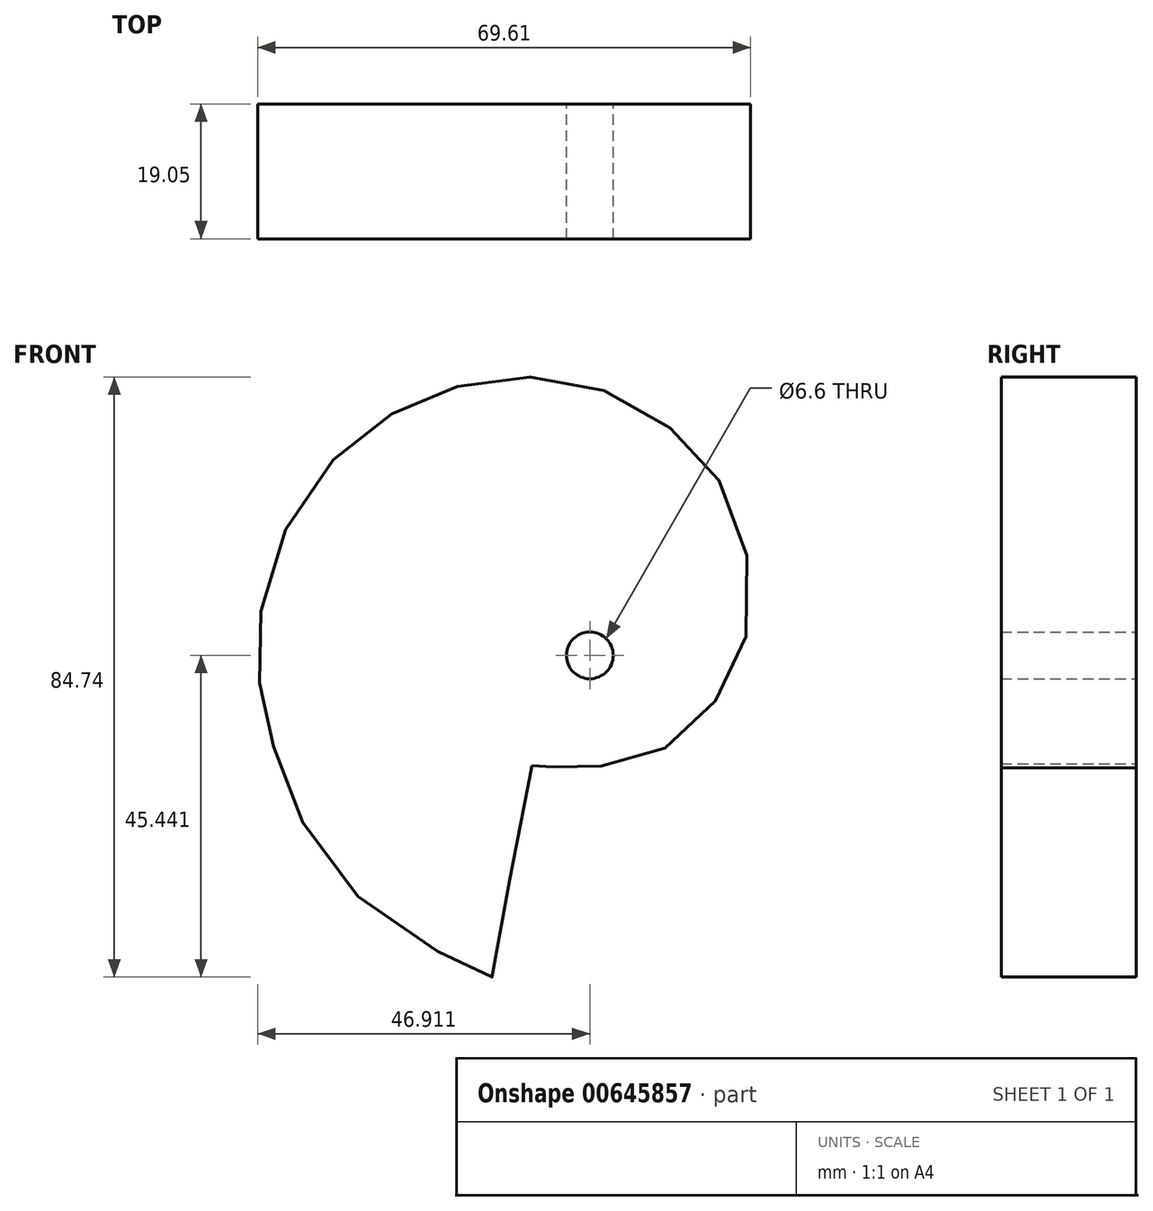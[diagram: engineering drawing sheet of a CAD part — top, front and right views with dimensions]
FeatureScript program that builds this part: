
annotation { "Feature Type Name" : "Feature", "Feature Type Description" : "" }
export const myFeature = defineFeature(function(context is Context, id is Id, definition is map)
    precondition{}
    {
        {
            var Q0;
            Q0=qCreatedBy(makeId("Front.planeOp"),FACE);
            var sketch = newSketch(context, id + "F0", { "sketchPlane" : qUnion([Q0])});
            skFitSpline(sketch, "E0", {"points": [v(-20.31, -30.06) * mm, v(-25.8, -59.84) * mm, v(-26.18, -59.78) * mm, v(-38.19, -53.84) * mm, v(-52.45, -38.51) * mm, v(-57.51, -24.56) * mm, v(-59.02, -15.14) * mm, v(-56.45, 0) * mm, v(-47.33, 14.14) * mm, v(-36.93, 21.2) * mm, v(-25.11, 24.54) * mm, v(-11.89, 23.51) * mm, v(0, 16.96) * mm, v(7.76, 7.2) * mm, v(10.46, -8.72) * mm, v(6.1, -20.28) * mm, v(-2.25, -27.99) * mm, v(-12.01, -30.3) * mm, v(-17.15, -30.3) * mm, v(-19, -30.03) * mm, v(-19.7, -29.91) * mm, v(-20.31, -30.06) * mm]});
            skCircle(sketch, "E1", {"center": v(-12.12, -14.5) * mm, "radius": 3.3 * mm});
            skSolve(sketch);
        }
        {
            var Q0;
            Q0 = qSketchRegion(id + "F0", true);
            extrude(context, id + "F1", {"entities" : qUnion([Q0]), "depth" : 19.05 * mm, "offsetDistance" : 25.4 * mm});
        }
    });
